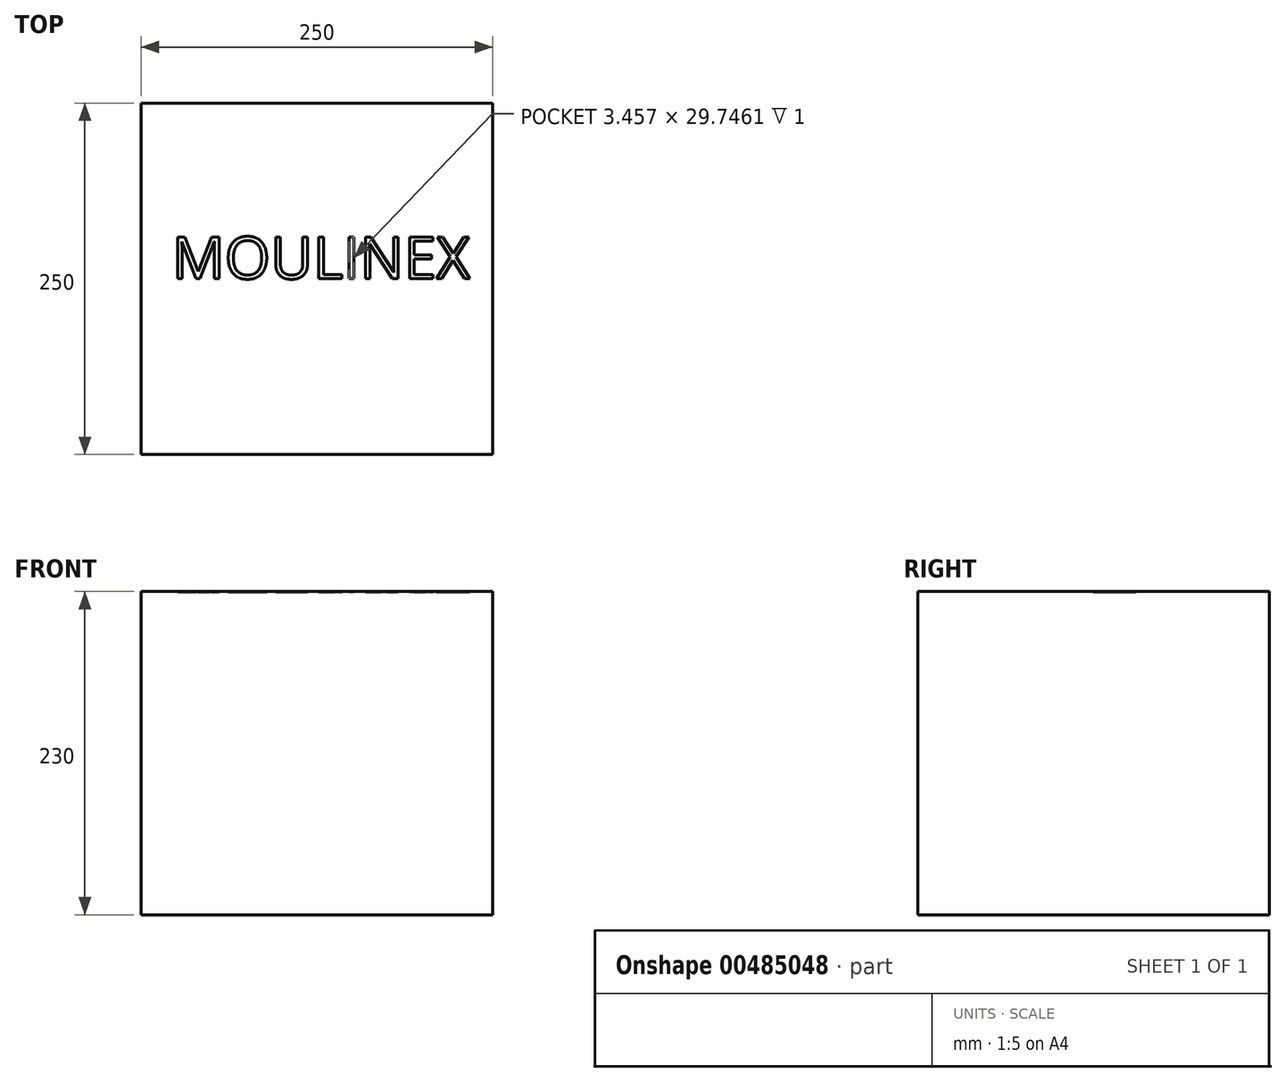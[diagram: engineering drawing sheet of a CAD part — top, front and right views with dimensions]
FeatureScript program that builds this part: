
annotation { "Feature Type Name" : "Feature", "Feature Type Description" : "" }
export const myFeature = defineFeature(function(context is Context, id is Id, definition is map)
    precondition{}
    {
        {
            var Q0;
            Q0=qCreatedBy(makeId("Top.planeOp"),FACE);
            var sketch = newSketch(context, id + "F0", { "sketchPlane" : qUnion([Q0])});
            skLineSegment(sketch, "E0.bottom", {"start": v(125, -125) * mm, "end": v(-125, -125) * mm});
            skLineSegment(sketch, "E0.top", {"start": v(125, 125) * mm, "end": v(-125, 125) * mm});
            skLineSegment(sketch, "E0.left", {"start": v(125, -125) * mm, "end": v(125, 125) * mm});
            skLineSegment(sketch, "E0.right", {"start": v(-125, -125) * mm, "end": v(-125, 125) * mm});
            skPoint(sketch, "E0.middle", {"position": v(0, 0) * mm});
            skSolve(sketch);
        }
        {
            var Q0;
            Q0 = qSketchRegion(id + "F0", true);
            extrude(context, id + "F1", {"entities" : qUnion([Q0]), "depth" : 230 * mm});
        }
        {
            var Q0;
            Q0=makeQuery(id+"F1.opExtrude","CAP_FACE",FACE,{"disambiguationData":[OSD([sQuery(id+"F0.wireOp",EDGE,"E0.bottom"),sQuery(id+"F0.wireOp",EDGE,"E0.top"),sQuery(id+"F0.wireOp",EDGE,"E0.left"),sQuery(id+"F0.wireOp",EDGE,"E0.right")])],"isStart":false});
            var sketch = newSketch(context, id + "F2", { "sketchPlane" : qUnion([Q0])});
            skText(sketch, "E1", { "text": "MOULINEX", "fontName": "OpenSans-Regular.ttf"});
            const initialGuessF2  = {"E1": [-0.10317, 0, 1, 0, 0.03]};
            skSetInitialGuess(sketch, initialGuessF2);
            skSolve(sketch);
        }
        {
            var Q0;
            Q0 = qSketchRegion(id + "F2", true);
            extrude(context, id + "F3", {"entities" : qUnion([Q0]), "operationType" : NewBodyOperationType.REMOVE, "oppositeDirection" : true, "depth" : 1 * mm});
        }
    });
